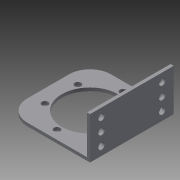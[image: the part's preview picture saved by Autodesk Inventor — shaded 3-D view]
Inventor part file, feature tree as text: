
AUTODESK INVENTOR PART (.ipt)
format: ipt  version: 2015 (Build 190159000, 159)  size: 141,824 bytes
history: native  units: in
note: dims shown in document units (in); Inventor stores cm internally (conversion verified against a paired STEP export)
features: extrude x3, sketch x2, fillet x1
ambient origin geometry x8: Origin, YZ Plane, XZ Plane, XY Plane, X Axis, Y Axis, Z Axis, Center Point
bodies: Solid1 (feature_tree)
feature tree (6):
  sketch  "Sketch1"  dims[d0=1.5748in d2=0.0591in]
  extrude  "Extrusion1"  Depth=0.0591in
  extrude  "Extrusion2"  Depth=0.3937in
  extrude  "Extrusion3"  Depth=0.3937in
  fillet  "Fillet1"  Radius=0.1181in
  sketch  "Sketch2"  dims[d7=0.1181in d8=0.1181in d9=0.1181in d10=0.1181in d11=0.1181in d12=0.1181in d13=0.0591in d14=0.0in d15=0.7874in d16=0.0in d17=0.2165in d18=1.3583in d19=0.1575in d20=0.2362in d21=0.2362in d22=0.1575in d23=0.2362in d24=0.2362in d25=0.1181in d26=0.1181in d27=0.1181in d28=0.1181in d29=0.1181in d30=0.1181in d31=0.1969in d32=0.0in d33=0.3937in]
